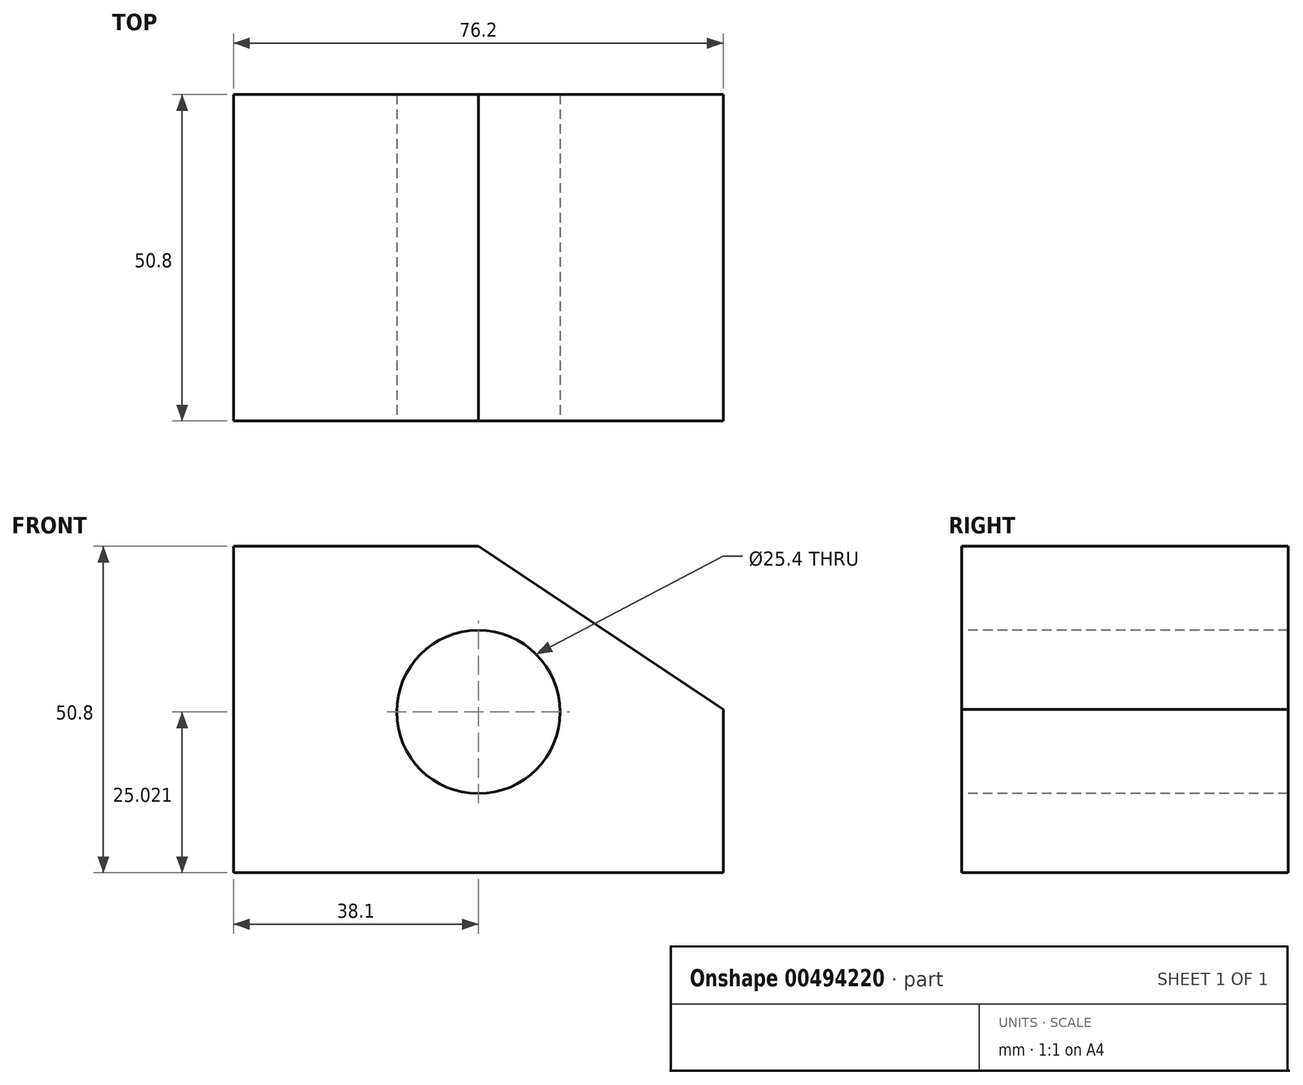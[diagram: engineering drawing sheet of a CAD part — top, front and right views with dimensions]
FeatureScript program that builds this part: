
annotation { "Feature Type Name" : "Feature", "Feature Type Description" : "" }
export const myFeature = defineFeature(function(context is Context, id is Id, definition is map)
    precondition{}
    {
        {
            var Q0;
            Q0=qCreatedBy(makeId("Front.planeOp"),FACE);
            var sketch = newSketch(context, id + "F0", { "sketchPlane" : qUnion([Q0])});
            skLineSegment(sketch, "E0.bottom", {"start": v(0, 50.8) * mm, "end": v(38.1, 50.8) * mm});
            skLineSegment(sketch, "E0.top", {"start": v(0, 0) * mm, "end": v(76.2, 0) * mm});
            skLineSegment(sketch, "E0.left", {"start": v(0, 50.8) * mm, "end": v(0, 0) * mm});
            skLineSegment(sketch, "E0.right", {"start": v(76.2, 25.4) * mm, "end": v(76.2, 0) * mm});
            skLineSegment(sketch, "E1", {"start": v(38.1, 50.8) * mm, "end": v(76.2, 25.4) * mm});
            skCircle(sketch, "E2", {"center": v(38.1, 25.02) * mm, "radius": 12.7 * mm});
            skPoint(sketch, "E2.centerSnap0", {"position": v(38.1, 0) * mm});
            skPoint(sketch, "E3.orphan", {"position": v(76.2, 50.8) * mm});
            skSolve(sketch);
        }
        {
            var Q0;
            Q0 = qSketchRegion(id + "F0", true);
            extrude(context, id + "F1", {"entities" : qUnion([Q0]), "oppositeDirection" : true, "depth" : 50.8 * mm});
        }
        {
            var Q0;
            Q0=makeQuery(id+"F1.opExtrude","CAP_FACE",FACE,{"disambiguationData":[OSD([sQuery(id+"F0.wireOp",EDGE,"E0.bottom"),sQuery(id+"F0.wireOp",EDGE,"E0.top"),sQuery(id+"F0.wireOp",EDGE,"E0.left"),sQuery(id+"F0.wireOp",EDGE,"E0.right"),sQuery(id+"F0.wireOp",EDGE,"E1"),sQuery(id+"F0.wireOp",EDGE,"E2")])],"isStart":true});
            extrude(context, id + "F2", {"entities" : qUnion([Q0]), "operationType" : NewBodyOperationType.ADD, "oppositeDirection" : true, "depth" : 50.8 * mm});
        }
    });
